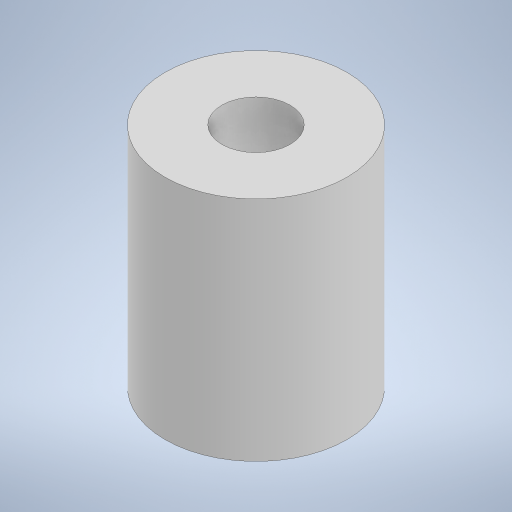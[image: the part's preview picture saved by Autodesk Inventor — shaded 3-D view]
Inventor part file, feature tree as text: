
AUTODESK INVENTOR PART (.ipt)
format: ipt  version: 2024.2 (Build 282272000, 272)  size: 215,040 bytes
history: native  units: mm
features: extrude x2, sketch x2
ambient origin geometry x8: Origin, YZ Plane, XZ Plane, XY Plane, X Axis, Y Axis, Z Axis, Center Point
bodies: Solid1 (feature_tree)
feature tree (4):
  extrude  "Extrusion1"  Depth=6.0mm
  extrude  "Extrusion2"  Depth=3.0mm
  sketch  "Sketch1"  dims[d0=8.0mm d1=6.0mm]
  sketch  "Sketch2"  dims[d2=5.0mm d3=0.0mm d4=3.0mm d5=8.0mm d6=5.0mm d7=0.0mm]
